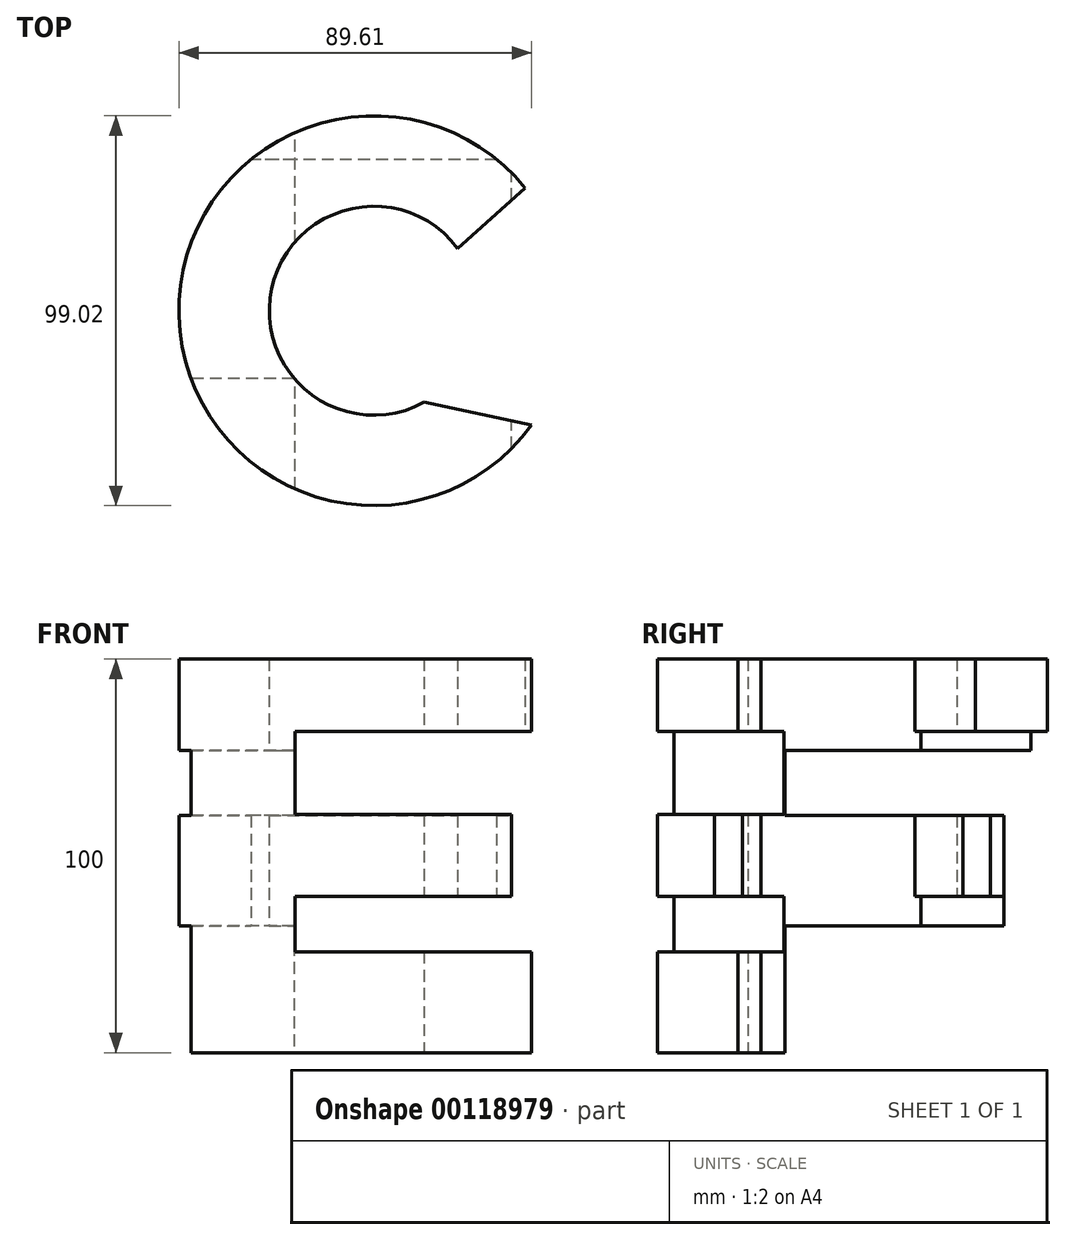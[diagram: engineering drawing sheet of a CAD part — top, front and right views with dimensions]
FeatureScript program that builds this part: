
annotation { "Feature Type Name" : "Feature", "Feature Type Description" : "" }
export const myFeature = defineFeature(function(context is Context, id is Id, definition is map)
    precondition{}
    {
        {
            var Q0;
            Q0=qCreatedBy(makeId("Top.planeOp"),FACE);
            var sketch = newSketch(context, id + "F0", { "sketchPlane" : qUnion([Q0])});
            skLineSegment(sketch, "E0.bottom", {"start": v(-50, 50) * mm, "end": v(50, 50) * mm, "construction": true});
            skLineSegment(sketch, "E0.top", {"start": v(-50, -50) * mm, "end": v(50, -50) * mm, "construction": true});
            skLineSegment(sketch, "E0.left", {"start": v(-50, 50) * mm, "end": v(-50, -50) * mm, "construction": true});
            skLineSegment(sketch, "E0.right", {"start": v(50, 50) * mm, "end": v(50, -50) * mm, "construction": true});
            skPoint(sketch, "E0.middle", {"position": v(0, 0) * mm});
            skArc(sketch, "E1", {"start": v(38.46, 31.19) * mm, "mid": v(-49.5, -1.35) * mm, "end": v(40.1, -29.04) * mm});
            skArc(sketch, "E2", {"start": v(21.3, 15.84) * mm, "mid": v(-25.94, 5.64) * mm, "end": v(12.8, -23.25) * mm});
            skLineSegment(sketch, "E3", {"start": v(21.3, 15.84) * mm, "end": v(38.46, 31.19) * mm});
            skLineSegment(sketch, "E4", {"start": v(12.8, -23.25) * mm, "end": v(40.1, -29.04) * mm});
            skSolve(sketch);
        }
        {
            var Q0;
            Q0=qCreatedBy(makeId("Front.planeOp"),FACE);
            var sketch = newSketch(context, id + "F1", { "sketchPlane" : qUnion([Q0])});
            skLineSegment(sketch, "E5.bottom", {"start": v(-50, -50) * mm, "end": v(-50, 50) * mm, "construction": true});
            skLineSegment(sketch, "E5.top", {"start": v(50, -50) * mm, "end": v(-50, -50) * mm, "construction": true});
            skLineSegment(sketch, "E5.left", {"start": v(50, 50) * mm, "end": v(50, -50) * mm, "construction": true});
            skLineSegment(sketch, "E5.right", {"start": v(-50, 50) * mm, "end": v(-50, -50) * mm, "construction": true});
            skPoint(sketch, "E5.middle", {"position": v(0, 0) * mm});
            skLineSegment(sketch, "E6.bottom", {"start": v(-50, 50) * mm, "end": v(-20, 50) * mm});
            skLineSegment(sketch, "E6.top", {"start": v(-50, -50) * mm, "end": v(-20, -50) * mm});
            skLineSegment(sketch, "E6.left", {"start": v(-50, 50) * mm, "end": v(-50, -50) * mm});
            skLineSegment(sketch, "E6.right", {"start": v(-20, 31.59) * mm, "end": v(-20, 10.47) * mm});
            skLineSegment(sketch, "E7.bottom", {"start": v(-20, 50) * mm, "end": v(50, 50) * mm});
            skLineSegment(sketch, "E7.top", {"start": v(-20, 31.59) * mm, "end": v(50, 31.59) * mm});
            skLineSegment(sketch, "E7.right", {"start": v(50, 50) * mm, "end": v(50, 31.59) * mm});
            skLineSegment(sketch, "E8.bottom", {"start": v(-20, 10.47) * mm, "end": v(35, 10.47) * mm});
            skLineSegment(sketch, "E8.top", {"start": v(-20, -10.24) * mm, "end": v(35, -10.24) * mm});
            skLineSegment(sketch, "E8.right", {"start": v(35, 10.47) * mm, "end": v(35, -10.24) * mm});
            skLineSegment(sketch, "E9.bottom", {"start": v(-20, -24.38) * mm, "end": v(50, -24.38) * mm});
            skLineSegment(sketch, "E9.top", {"start": v(-20, -50) * mm, "end": v(50, -50) * mm});
            skLineSegment(sketch, "E9.right", {"start": v(50, -24.38) * mm, "end": v(50, -50) * mm});
            skLineSegment(sketch, "E10.trimOffspring", {"start": v(-20, -10.24) * mm, "end": v(-20, -24.38) * mm});
            skLineSegment(sketch, "E11.trimOffspring", {"start": v(-20, -50) * mm, "end": v(-20, -50) * mm});
            skSolve(sketch);
        }
        {
            var Q0;
            Q0=qCreatedBy(makeId("Right.planeOp"),FACE);
            var sketch = newSketch(context, id + "F2", { "sketchPlane" : qUnion([Q0])});
            skLineSegment(sketch, "E12.bottom", {"start": v(49.9, 50.52) * mm, "end": v(-49.9, 50.52) * mm, "construction": true});
            skLineSegment(sketch, "E12.top", {"start": v(49.9, -50.52) * mm, "end": v(-49.9, -50.52) * mm, "construction": true});
            skLineSegment(sketch, "E12.left", {"start": v(49.9, 50.52) * mm, "end": v(49.9, -50.52) * mm, "construction": true});
            skLineSegment(sketch, "E12.right", {"start": v(-49.9, 50.52) * mm, "end": v(-49.9, -50.52) * mm, "construction": true});
            skPoint(sketch, "E12.middle", {"position": v(0, 0) * mm});
            skLineSegment(sketch, "E13.bottom", {"start": v(49.9, 50.52) * mm, "end": v(-49.9, 50.52) * mm});
            skLineSegment(sketch, "E13.top", {"start": v(49.9, 26.8) * mm, "end": v(-17.18, 26.8) * mm});
            skLineSegment(sketch, "E13.left", {"start": v(49.9, 50.52) * mm, "end": v(49.9, 26.8) * mm});
            skLineSegment(sketch, "E13.right", {"start": v(-49.9, 50.52) * mm, "end": v(-49.9, 26.8) * mm});
            skLineSegment(sketch, "E14.top", {"start": v(-17.18, -50.52) * mm, "end": v(-49.9, -50.52) * mm});
            skLineSegment(sketch, "E14.left", {"start": v(-17.18, 26.8) * mm, "end": v(-17.18, 10.22) * mm});
            skLineSegment(sketch, "E14.right", {"start": v(-49.9, 26.8) * mm, "end": v(-49.9, -50.52) * mm});
            skLineSegment(sketch, "E15.bottom", {"start": v(38.45, 0) * mm, "end": v(0, 0) * mm});
            skLineSegment(sketch, "E15.top", {"start": v(38.45, -17.8) * mm, "end": v(-17.18, -17.8) * mm});
            skLineSegment(sketch, "E15.left", {"start": v(38.45, 0) * mm, "end": v(38.45, -17.8) * mm});
            skLineSegment(sketch, "E16.trimOffspring", {"start": v(-17.18, -17.8) * mm, "end": v(-17.18, -50.52) * mm});
            skLineSegment(sketch, "E17", {"start": v(38.45, 0) * mm, "end": v(38.45, 10.22) * mm});
            skLineSegment(sketch, "E18", {"start": v(38.45, 10.22) * mm, "end": v(-17.18, 10.22) * mm});
            skSolve(sketch);
        }
        {
            var Q0;
            Q0 = qSketchRegion(id + "F0", true);
            extrude(context, id + "F3", {"entities" : qUnion([Q0]), "endBound" : BoundingType.SYMMETRIC, "depth" : 100 * mm});
        }
        {
            var Q0;
            Q0 = qSketchRegion(id + "F1", true);
            extrude(context, id + "F4", {"entities" : qUnion([Q0]), "operationType" : NewBodyOperationType.INTERSECT, "endBound" : BoundingType.SYMMETRIC, "depth" : 100 * mm});
        }
        {
            var Q0;
            Q0 = qSketchRegion(id + "F2", true);
            extrude(context, id + "F5", {"entities" : qUnion([Q0]), "operationType" : NewBodyOperationType.INTERSECT, "endBound" : BoundingType.SYMMETRIC, "depth" : 100 * mm});
        }
    });
